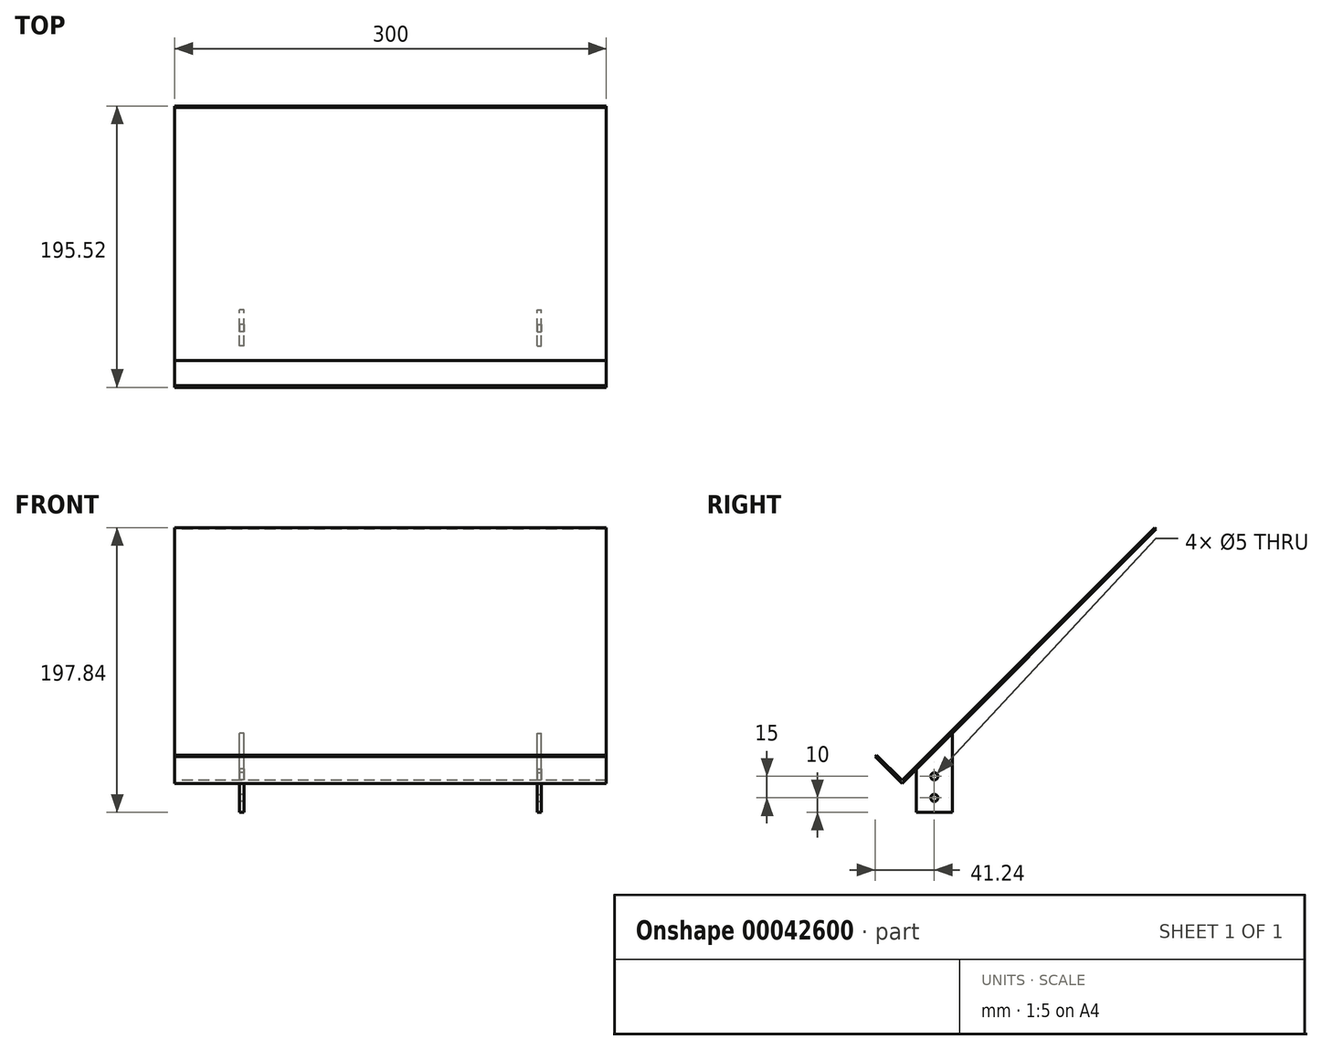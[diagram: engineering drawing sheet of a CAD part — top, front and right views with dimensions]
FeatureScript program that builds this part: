
annotation { "Feature Type Name" : "Feature", "Feature Type Description" : "" }
export const myFeature = defineFeature(function(context is Context, id is Id, definition is map)
    precondition{}
    {
        {
            var Q0;
            Q0=qCreatedBy(makeId("Right.planeOp"),FACE);
            var sketch = newSketch(context, id + "F0", { "sketchPlane" : qUnion([Q0])});
            skLineSegment(sketch, "E0", {"start": v(0, 0) * mm, "end": v(176.78, 176.78) * mm});
            skLineSegment(sketch, "E1", {"start": v(176.78, 176.78) * mm, "end": v(175.72, 177.84) * mm});
            skLineSegment(sketch, "E2", {"start": v(175.72, 177.84) * mm, "end": v(-1.06, 1.06) * mm});
            skLineSegment(sketch, "E3", {"start": v(-1.06, 1.06) * mm, "end": v(0, 0) * mm});
            skLineSegment(sketch, "E4", {"start": v(10, 10) * mm, "end": v(10, -20) * mm});
            skLineSegment(sketch, "E5", {"start": v(10, -20) * mm, "end": v(35, -20) * mm});
            skLineSegment(sketch, "E6", {"start": v(35, -20) * mm, "end": v(35, 35) * mm});
            skLineSegment(sketch, "E7", {"start": v(22.5, -20) * mm, "end": v(22.5, 22.5) * mm, "construction": true});
            skCircle(sketch, "E8", {"center": v(22.5, 5) * mm, "radius": 2.5 * mm});
            skCircle(sketch, "E9", {"center": v(22.5, -10) * mm, "radius": 2.5 * mm});
            skLineSegment(sketch, "E10", {"start": v(-1.06, 1.06) * mm, "end": v(-18.74, 18.74) * mm});
            skLineSegment(sketch, "E11", {"start": v(-18.74, 18.74) * mm, "end": v(-17.68, 19.8) * mm});
            skLineSegment(sketch, "E12", {"start": v(-17.68, 19.8) * mm, "end": v(0, 2.12) * mm});
            skSolve(sketch);
        }
        {
            var Q0;
            {var subQ4=sQuery(id+"F0.wireOp",EDGE,"E1");Q0=makeQuery(id+"F0.imprint","IMPRINT",FACE,{"disambiguationData":[TD([[makeQuery(id+"F0.imprint","IMPRINT",EDGE,{"derivedFrom":subQ4}),1.0]])]});}
            var Q1;
            {var subQ1=sQuery(id+"F0.wireOp",EDGE,"E10");Q1=makeQuery(id+"F0.imprint","IMPRINT",FACE,{"disambiguationData":[TD([[makeQuery(id+"F0.imprint","IMPRINT",EDGE,{"derivedFrom":subQ1}),-1.0]])]});}
            extrude(context, id + "F1", {"entities" : qUnion([Q0, Q1]), "endBound" : BoundingType.SYMMETRIC, "depth" : 300 * mm});
        }
        {
            var Q0;
            {var subQ0=sQuery(id+"F0.wireOp",EDGE,"E4");Q0=makeQuery(id+"F0.imprint","IMPRINT",FACE,{"disambiguationData":[TD([[makeQuery(id+"F0.imprint","IMPRINT",EDGE,{"derivedFrom":subQ0}),1.0]])]});}
            extrude(context, id + "F2", {"entities" : qUnion([Q0]), "oppositeDirection" : true, "depth" : 3 * mm});
        }
        {
            var Q0;
            Q0=makeQuery(id+"F2.opExtrude","SWEPT_BODY",BODY,{"disambiguationData":[OSD([sQuery(id+"F0.wireOp",EDGE,"E0"),sQuery(id+"F0.wireOp",EDGE,"E4"),sQuery(id+"F0.wireOp",EDGE,"E5"),sQuery(id+"F0.wireOp",EDGE,"E6"),sQuery(id+"F0.wireOp",EDGE,"E8"),sQuery(id+"F0.wireOp",EDGE,"E9")])]});
            transform(context, id + "F3", {"entities" : qUnion([Q0]), "transformType" : TransformType.TRANSLATION_3D, "dx" : 105 * mm, "dy" : 0 * mm, "dz" : 0 * mm, "makeCopy" : false});
        }
        {
            var Q0;
            Q0=makeQuery(id+"F2.opExtrude","SWEPT_BODY",BODY,{"disambiguationData":[OSD([sQuery(id+"F0.wireOp",EDGE,"E0"),sQuery(id+"F0.wireOp",EDGE,"E4"),sQuery(id+"F0.wireOp",EDGE,"E5"),sQuery(id+"F0.wireOp",EDGE,"E6"),sQuery(id+"F0.wireOp",EDGE,"E8"),sQuery(id+"F0.wireOp",EDGE,"E9")])]});
            var Q1;
            Q1=qCreatedBy(makeId("Right.planeOp"),FACE);
            mirror(context, id + "F4", {"operationType" : NewBodyOperationType.ADD, "entities" : qUnion([Q0]), "mirrorPlane" : qUnion([Q1])});
        }
    });
